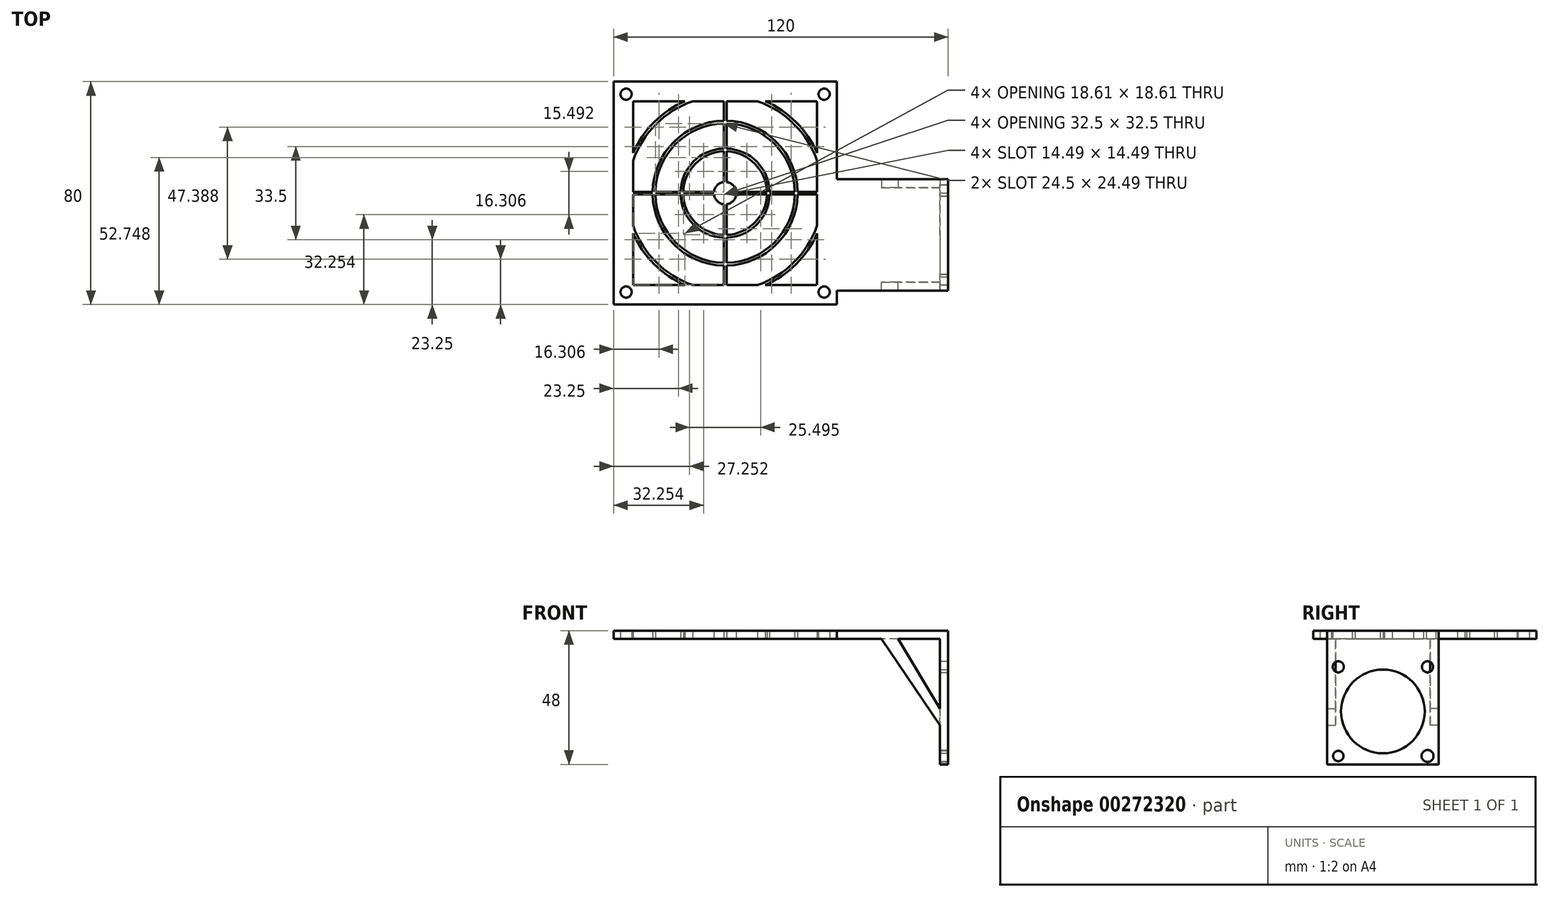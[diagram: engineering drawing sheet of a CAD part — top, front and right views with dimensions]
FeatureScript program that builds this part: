
annotation { "Feature Type Name" : "Feature", "Feature Type Description" : "" }
export const myFeature = defineFeature(function(context is Context, id is Id, definition is map)
    precondition{}
    {
        {
            var Q0;
            Q0=qCreatedBy(makeId("Top.planeOp"),FACE);
            var sketch = newSketch(context, id + "F0", { "sketchPlane" : qUnion([Q0])});
            skLineSegment(sketch, "E0.bottom", {"start": v(-80, 0) * mm, "end": v(0, 0) * mm});
            skLineSegment(sketch, "E0.top", {"start": v(-80, -80) * mm, "end": v(0, -80) * mm});
            skLineSegment(sketch, "E0.left", {"start": v(-80, 0) * mm, "end": v(-80, -80) * mm});
            skLineSegment(sketch, "E0.right", {"start": v(0, 0) * mm, "end": v(0, -80) * mm});
            skLineSegment(sketch, "E1", {"start": v(0, -35) * mm, "end": v(40, -35) * mm});
            skLineSegment(sketch, "E2", {"start": v(40, -35) * mm, "end": v(40, -75) * mm});
            skLineSegment(sketch, "E3", {"start": v(40, -75) * mm, "end": v(0, -75) * mm});
            skLineSegment(sketch, "E4", {"start": v(-80, -40) * mm, "end": v(0, -40) * mm, "construction": true});
            skLineSegment(sketch, "E5", {"start": v(40, -55) * mm, "end": v(0, -55) * mm, "construction": true});
            skLineSegment(sketch, "E6.0", {"start": v(-73, -7) * mm, "end": v(-7, -7) * mm});
            skLineSegment(sketch, "E6.1", {"start": v(-73, -7) * mm, "end": v(-73, -73) * mm});
            skLineSegment(sketch, "E6.2", {"start": v(-73, -73) * mm, "end": v(-7, -73) * mm});
            skLineSegment(sketch, "E6.3", {"start": v(-7, -7) * mm, "end": v(-7, -73) * mm});
            skCircle(sketch, "E7", {"center": v(-75.5, -4.5) * mm, "radius": 2 * mm});
            skCircle(sketch, "E8", {"center": v(-4.5, -4.5) * mm, "radius": 2 * mm});
            skCircle(sketch, "E9", {"center": v(-75.5, -75.5) * mm, "radius": 2 * mm});
            skCircle(sketch, "E10", {"center": v(-4.5, -75.5) * mm, "radius": 2 * mm});
            skLineSegment(sketch, "E11", {"start": v(-75.5, -4.5) * mm, "end": v(-4.5, -4.5) * mm, "construction": true});
            skLineSegment(sketch, "E12", {"start": v(-40, 0) * mm, "end": v(-40, -80) * mm, "construction": true});
            skPoint(sketch, "E13", {"position": v(-40, -4.5) * mm});
            skLineSegment(sketch, "E14", {"start": v(-75.5, -4.5) * mm, "end": v(-75.5, -75.5) * mm, "construction": true});
            skLineSegment(sketch, "E15", {"start": v(-75.5, -75.5) * mm, "end": v(-4.5, -75.5) * mm, "construction": true});
            skPoint(sketch, "E16", {"position": v(-75.5, -40) * mm});
            skSolve(sketch);
        }
        {
            var Q0;
            {var subQ4=sQuery(id+"F0.wireOp",EDGE,"E0.bottom");Q0=makeQuery(id+"F0.imprint","IMPRINT",FACE,{"disambiguationData":[TD([[makeQuery(id+"F0.imprint","IMPRINT",EDGE,{"derivedFrom":subQ4}),-1.0]])]});}
            var Q1;
            {var subQ0=sQuery(id+"F0.wireOp",EDGE,"E1");Q1=makeQuery(id+"F0.imprint","IMPRINT",FACE,{"disambiguationData":[TD([[makeQuery(id+"F0.imprint","IMPRINT",EDGE,{"derivedFrom":subQ0}),-1.0]])]});}
            extrude(context, id + "F1", {"entities" : qUnion([Q0, Q1]), "depth" : 3 * mm});
        }
        {
            var Q0;
            Q0=makeQuery(id+"F1.opExtrude","CAP_FACE",FACE,{"disambiguationData":[OSD([sQuery(id+"F0.wireOp",EDGE,"E0.bottom"),sQuery(id+"F0.wireOp",EDGE,"E0.top"),sQuery(id+"F0.wireOp",EDGE,"E0.left"),sQuery(id+"F0.wireOp",EDGE,"E0.right"),sQuery(id+"F0.wireOp",EDGE,"E1"),sQuery(id+"F0.wireOp",EDGE,"E2"),sQuery(id+"F0.wireOp",EDGE,"E3"),sQuery(id+"F0.wireOp",EDGE,"E6.0"),sQuery(id+"F0.wireOp",EDGE,"E6.1"),sQuery(id+"F0.wireOp",EDGE,"E6.2"),sQuery(id+"F0.wireOp",EDGE,"E6.3"),sQuery(id+"F0.wireOp",EDGE,"E7"),sQuery(id+"F0.wireOp",EDGE,"E8"),sQuery(id+"F0.wireOp",EDGE,"E9"),sQuery(id+"F0.wireOp",EDGE,"E10")])],"isStart":true});
            var sketch = newSketch(context, id + "F2", { "sketchPlane" : qUnion([Q0])});
            skLineSegment(sketch, "E17.bottom", {"start": v(40, 35) * mm, "end": v(37, 35) * mm});
            skLineSegment(sketch, "E17.top", {"start": v(40, 75) * mm, "end": v(37, 75) * mm});
            skLineSegment(sketch, "E17.left", {"start": v(40, 35) * mm, "end": v(40, 75) * mm});
            skLineSegment(sketch, "E17.right", {"start": v(37, 35) * mm, "end": v(37, 75) * mm});
            skSolve(sketch);
        }
        {
            var Q0;
            Q0=makeQuery(id+"F2.imprint","IMPRINT",FACE,{"disambiguationData":[TD([[makeQuery(id+"F2.imprint","IMPRINT",EDGE,{"derivedFrom":sQuery(id+"F2.wireOp",EDGE,"E17.bottom")}),1.0]])]});
            extrude(context, id + "F3", {"entities" : qUnion([Q0]), "operationType" : NewBodyOperationType.ADD, "depth" : 45 * mm});
        }
        {
            var Q0;
            Q0=makeQuery(id+"F3.boolean.opBoolean","MERGE",FACE,{"derivedFrom":[makeQuery(id+"F1.opExtrude","SWEPT_FACE",FACE,{"disambiguationData":[OSD([sQuery(id+"F0.wireOp",EDGE,"E2")])]}),makeQuery(id+"F3.opExtrude","SWEPT_FACE",FACE,{"disambiguationData":[OSD([sQuery(id+"F2.wireOp",EDGE,"E17.left")])]})]});
            var sketch = newSketch(context, id + "F4", { "sketchPlane" : qUnion([Q0])});
            skLineSegment(sketch, "E18", {"start": v(-55, -45) * mm, "end": v(-55, 3) * mm, "construction": true});
            skCircle(sketch, "E19", {"center": v(-71, -10) * mm, "radius": 2 * mm});
            skCircle(sketch, "E20", {"center": v(-39, -10) * mm, "radius": 2 * mm});
            skCircle(sketch, "E21", {"center": v(-71, -42) * mm, "radius": 1.86 * mm});
            skCircle(sketch, "E22", {"center": v(-39, -42) * mm, "radius": 2.14 * mm});
            skLineSegment(sketch, "E23", {"start": v(-71, -10) * mm, "end": v(-39, -10) * mm, "construction": true});
            skPoint(sketch, "E24", {"position": v(-55, -10) * mm});
            skLineSegment(sketch, "E25", {"start": v(-71, -10) * mm, "end": v(-71, -42) * mm, "construction": true});
            skLineSegment(sketch, "E26", {"start": v(-71, -42) * mm, "end": v(-39, -42) * mm, "construction": true});
            skLineSegment(sketch, "E27", {"start": v(-75, -26) * mm, "end": v(-35, -26) * mm, "construction": true});
            skPoint(sketch, "E27.startSnap0", {"position": v(-71, -26) * mm});
            skPoint(sketch, "E27.startSnap1", {"position": v(-75, -21) * mm});
            skCircle(sketch, "E28", {"center": v(-55, -26) * mm, "radius": 15 * mm});
            skSolve(sketch);
        }
        {
            var Q0;
            Q0=makeQuery(id+"F4.imprint","IMPRINT",FACE,{"disambiguationData":[TD([[makeQuery(id+"F4.imprint","IMPRINT",EDGE,{"derivedFrom":sQuery(id+"F4.wireOp",EDGE,"E19")}),1.0]])]});
            var Q1;
            Q1=makeQuery(id+"F4.imprint","IMPRINT",FACE,{"disambiguationData":[TD([[makeQuery(id+"F4.imprint","IMPRINT",EDGE,{"derivedFrom":sQuery(id+"F4.wireOp",EDGE,"E21")}),1.0]])]});
            var Q2;
            Q2=makeQuery(id+"F4.imprint","IMPRINT",FACE,{"disambiguationData":[TD([[makeQuery(id+"F4.imprint","IMPRINT",EDGE,{"derivedFrom":sQuery(id+"F4.wireOp",EDGE,"E28")}),1.0]])]});
            var Q3;
            Q3=makeQuery(id+"F4.imprint","IMPRINT",FACE,{"disambiguationData":[TD([[makeQuery(id+"F4.imprint","IMPRINT",EDGE,{"derivedFrom":sQuery(id+"F4.wireOp",EDGE,"E22")}),1.0]])]});
            var Q4;
            Q4=makeQuery(id+"F4.imprint","IMPRINT",FACE,{"disambiguationData":[TD([[makeQuery(id+"F4.imprint","IMPRINT",EDGE,{"derivedFrom":sQuery(id+"F4.wireOp",EDGE,"E20")}),1.0]])]});
            extrude(context, id + "F5", {"entities" : qUnion([Q0, Q1, Q2, Q3, Q4]), "operationType" : NewBodyOperationType.REMOVE, "oppositeDirection" : true, "depth" : 25 * mm});
        }
        {
            var Q0;
            Q0=makeQuery(id+"F1.opExtrude","CAP_FACE",FACE,{"disambiguationData":[OSD([sQuery(id+"F0.wireOp",EDGE,"E0.bottom"),sQuery(id+"F0.wireOp",EDGE,"E0.top"),sQuery(id+"F0.wireOp",EDGE,"E0.left"),sQuery(id+"F0.wireOp",EDGE,"E0.right"),sQuery(id+"F0.wireOp",EDGE,"E1"),sQuery(id+"F0.wireOp",EDGE,"E2"),sQuery(id+"F0.wireOp",EDGE,"E3"),sQuery(id+"F0.wireOp",EDGE,"E6.0"),sQuery(id+"F0.wireOp",EDGE,"E6.1"),sQuery(id+"F0.wireOp",EDGE,"E6.2"),sQuery(id+"F0.wireOp",EDGE,"E6.3"),sQuery(id+"F0.wireOp",EDGE,"E7"),sQuery(id+"F0.wireOp",EDGE,"E8"),sQuery(id+"F0.wireOp",EDGE,"E9"),sQuery(id+"F0.wireOp",EDGE,"E10")])],"isStart":true});
            var sketch = newSketch(context, id + "F6", { "sketchPlane" : qUnion([Q0])});
            skLineSegment(sketch, "E29", {"start": v(-73, 40) * mm, "end": v(-44, 40) * mm, "construction": true});
            skLineSegment(sketch, "E30", {"start": v(-73, 39.5) * mm, "end": v(-71.5, 39.5) * mm});
            skLineSegment(sketch, "E31", {"start": v(-73, 40.5) * mm, "end": v(-71, 40.5) * mm});
            skLineSegment(sketch, "E32.0", {"start": v(-73, 7) * mm, "end": v(-73, 73) * mm});
            skLineSegment(sketch, "E32.1", {"start": v(-73, 7) * mm, "end": v(-7, 7) * mm});
            skLineSegment(sketch, "E32.2", {"start": v(-7, 7) * mm, "end": v(-7, 73) * mm});
            skLineSegment(sketch, "E32.3", {"start": v(-73, 73) * mm, "end": v(-7, 73) * mm});
            skLineSegment(sketch, "E33", {"start": v(-40, 73) * mm, "end": v(-40, 44) * mm, "construction": true});
            skLineSegment(sketch, "E34", {"start": v(-40.5, 7) * mm, "end": v(-40.5, 9) * mm});
            skLineSegment(sketch, "E35", {"start": v(-39.5, 73) * mm, "end": v(-39.5, 71) * mm});
            skArc(sketch, "E36", {"start": v(-36.03, 40.5) * mm, "mid": v(-37.17, 42.83) * mm, "end": v(-39.5, 43.97) * mm});
            skLineSegment(sketch, "E37.trimOffspring", {"start": v(-40.5, 43.97) * mm, "end": v(-40.5, 49.99) * mm});
            skLineSegment(sketch, "E38.trimOffspring", {"start": v(-40, 39.5) * mm, "end": v(-39, 39.5) * mm, "construction": true});
            skLineSegment(sketch, "E39.trimOffspring", {"start": v(-41, 40.5) * mm, "end": v(-40, 40.5) * mm, "construction": true});
            skLineSegment(sketch, "E40.trimOffspring", {"start": v(-41, 40) * mm, "end": v(-40, 40) * mm, "construction": true});
            skLineSegment(sketch, "E41.trimOffspring", {"start": v(-36.03, 40.5) * mm, "end": v(-30.01, 40.5) * mm});
            skLineSegment(sketch, "E42.trimOffspring", {"start": v(-36, 40) * mm, "end": v(-7, 40) * mm, "construction": true});
            skLineSegment(sketch, "E43.trimOffspring", {"start": v(-36.03, 39.5) * mm, "end": v(-30.01, 39.5) * mm});
            skLineSegment(sketch, "E44.trimOffspring", {"start": v(-39.5, 36.03) * mm, "end": v(-39.5, 30.01) * mm});
            skLineSegment(sketch, "E45.trimOffspring", {"start": v(-40, 40.5) * mm, "end": v(-40, 40) * mm, "construction": true});
            skLineSegment(sketch, "E46.trimOffspring", {"start": v(-40, 36) * mm, "end": v(-40, 7) * mm, "construction": true});
            skArc(sketch, "E47", {"start": v(-39.5, 25) * mm, "mid": v(-29.4, 29.4) * mm, "end": v(-25, 39.5) * mm});
            skArc(sketch, "E48", {"start": v(-39.5, 24) * mm, "mid": v(-28.69, 28.69) * mm, "end": v(-24, 39.5) * mm});
            skArc(sketch, "E49", {"start": v(-39.5, 15) * mm, "mid": v(-22.32, 22.32) * mm, "end": v(-15, 39.5) * mm});
            skArc(sketch, "E50", {"start": v(-39.5, 14) * mm, "mid": v(-21.62, 21.62) * mm, "end": v(-14, 39.5) * mm});
            skLineSegment(sketch, "E51.trimOffspring", {"start": v(-39.5, 9) * mm, "end": v(-39.5, 7) * mm});
            skLineSegment(sketch, "E52.trimOffspring", {"start": v(-40.5, 10) * mm, "end": v(-40.5, 14) * mm});
            skLineSegment(sketch, "E53.trimOffspring", {"start": v(-39.5, 14) * mm, "end": v(-39.5, 10) * mm});
            skLineSegment(sketch, "E54.trimOffspring", {"start": v(-40.5, 15) * mm, "end": v(-40.5, 19) * mm});
            skLineSegment(sketch, "E55.trimOffspring", {"start": v(-39.5, 19) * mm, "end": v(-39.5, 15) * mm});
            skLineSegment(sketch, "E56.trimOffspring", {"start": v(-40.5, 20) * mm, "end": v(-40.5, 24) * mm});
            skLineSegment(sketch, "E57.trimOffspring", {"start": v(-39.5, 24) * mm, "end": v(-39.5, 20) * mm});
            skLineSegment(sketch, "E58.trimOffspring", {"start": v(-40.5, 25) * mm, "end": v(-40.5, 29.01) * mm});
            skLineSegment(sketch, "E59.trimOffspring", {"start": v(-39.5, 29.01) * mm, "end": v(-39.5, 25) * mm});
            skLineSegment(sketch, "E60.trimOffspring", {"start": v(-40.5, 30.01) * mm, "end": v(-40.5, 36.03) * mm});
            skLineSegment(sketch, "E61.trimOffspring", {"start": v(-39.5, 49.99) * mm, "end": v(-39.5, 43.97) * mm});
            skLineSegment(sketch, "E62.trimOffspring", {"start": v(-40.5, 50.99) * mm, "end": v(-40.5, 55) * mm});
            skLineSegment(sketch, "E63.trimOffspring", {"start": v(-40.5, 56) * mm, "end": v(-40.5, 60) * mm});
            skLineSegment(sketch, "E64.trimOffspring", {"start": v(-39.5, 55) * mm, "end": v(-39.5, 50.99) * mm});
            skLineSegment(sketch, "E65.trimOffspring", {"start": v(-39.5, 60) * mm, "end": v(-39.5, 56) * mm});
            skLineSegment(sketch, "E66.trimOffspring", {"start": v(-40.5, 61) * mm, "end": v(-40.5, 65) * mm});
            skLineSegment(sketch, "E67.trimOffspring", {"start": v(-39.5, 65) * mm, "end": v(-39.5, 61) * mm});
            skLineSegment(sketch, "E68.trimOffspring", {"start": v(-40.5, 66) * mm, "end": v(-40.5, 70) * mm});
            skLineSegment(sketch, "E69.trimOffspring", {"start": v(-39.5, 70) * mm, "end": v(-39.5, 66) * mm});
            skLineSegment(sketch, "E70.trimOffspring", {"start": v(-40.5, 71) * mm, "end": v(-40.5, 73) * mm});
            skLineSegment(sketch, "E71.trimOffspring", {"start": v(-29.01, 39.5) * mm, "end": v(-25, 39.5) * mm});
            skLineSegment(sketch, "E72.trimOffspring", {"start": v(-29.01, 40.5) * mm, "end": v(-25, 40.5) * mm});
            skLineSegment(sketch, "E73.trimOffspring", {"start": v(-24, 40.5) * mm, "end": v(-20, 40.5) * mm});
            skLineSegment(sketch, "E74.trimOffspring", {"start": v(-24, 39.5) * mm, "end": v(-20, 39.5) * mm});
            skLineSegment(sketch, "E75.trimOffspring", {"start": v(-19, 39.5) * mm, "end": v(-15, 39.5) * mm});
            skLineSegment(sketch, "E76.trimOffspring", {"start": v(-19, 40.5) * mm, "end": v(-15, 40.5) * mm});
            skLineSegment(sketch, "E77.trimOffspring", {"start": v(-14, 40.5) * mm, "end": v(-10, 40.5) * mm});
            skLineSegment(sketch, "E78.trimOffspring", {"start": v(-14, 39.5) * mm, "end": v(-10, 39.5) * mm});
            skLineSegment(sketch, "E79.trimOffspring", {"start": v(-9, 39.5) * mm, "end": v(-7, 39.5) * mm});
            skLineSegment(sketch, "E80.trimOffspring", {"start": v(-9, 40.5) * mm, "end": v(-7, 40.5) * mm});
            skLineSegment(sketch, "E81.trimOffspring", {"start": v(-49.99, 40.5) * mm, "end": v(-43.97, 40.5) * mm});
            skLineSegment(sketch, "E82.trimOffspring", {"start": v(-49.99, 39.5) * mm, "end": v(-43.97, 39.5) * mm});
            skLineSegment(sketch, "E83.trimOffspring", {"start": v(-55, 39.5) * mm, "end": v(-50.99, 39.5) * mm});
            skLineSegment(sketch, "E84.trimOffspring", {"start": v(-55, 40.5) * mm, "end": v(-50.99, 40.5) * mm});
            skLineSegment(sketch, "E85.trimOffspring", {"start": v(-60, 40.5) * mm, "end": v(-56, 40.5) * mm});
            skLineSegment(sketch, "E86.trimOffspring", {"start": v(-60, 39.5) * mm, "end": v(-56, 39.5) * mm});
            skLineSegment(sketch, "E87.trimOffspring", {"start": v(-65, 39.5) * mm, "end": v(-61, 39.5) * mm});
            skLineSegment(sketch, "E88.trimOffspring", {"start": v(-65, 40.5) * mm, "end": v(-61, 40.5) * mm});
            skLineSegment(sketch, "E89.trimOffspring", {"start": v(-70, 40.5) * mm, "end": v(-66, 40.5) * mm});
            skLineSegment(sketch, "E90.trimOffspring", {"start": v(-70, 39.5) * mm, "end": v(-66, 39.5) * mm});
            skArc(sketch, "E91.trimOffspring", {"start": v(-55, 39.5) * mm, "mid": v(-50.6, 29.4) * mm, "end": v(-40.5, 25) * mm});
            skArc(sketch, "E92.trimOffspring", {"start": v(-56, 39.5) * mm, "mid": v(-51.31, 28.69) * mm, "end": v(-40.5, 24) * mm});
            skArc(sketch, "E93.trimOffspring", {"start": v(-65, 39.5) * mm, "mid": v(-57.68, 22.32) * mm, "end": v(-40.5, 15) * mm});
            skArc(sketch, "E94.trimOffspring", {"start": v(-66, 39.5) * mm, "mid": v(-58.38, 21.62) * mm, "end": v(-40.5, 14) * mm});
            skArc(sketch, "E95.trimOffspring", {"start": v(-40.5, 55) * mm, "mid": v(-50.6, 50.6) * mm, "end": v(-55, 40.5) * mm});
            skArc(sketch, "E96.trimOffspring", {"start": v(-40.5, 56) * mm, "mid": v(-51.31, 51.31) * mm, "end": v(-56, 40.5) * mm});
            skArc(sketch, "E97.trimOffspring", {"start": v(-40.5, 65) * mm, "mid": v(-57.68, 57.68) * mm, "end": v(-65, 40.5) * mm});
            skArc(sketch, "E98.trimOffspring", {"start": v(-40.5, 66) * mm, "mid": v(-58.38, 58.38) * mm, "end": v(-66, 40.5) * mm});
            skArc(sketch, "E99.trimOffspring", {"start": v(-25, 40.5) * mm, "mid": v(-29.4, 50.6) * mm, "end": v(-39.5, 55) * mm});
            skArc(sketch, "E100.trimOffspring", {"start": v(-24, 40.5) * mm, "mid": v(-28.69, 51.31) * mm, "end": v(-39.5, 56) * mm});
            skArc(sketch, "E101.trimOffspring", {"start": v(-15, 40.5) * mm, "mid": v(-22.32, 57.68) * mm, "end": v(-39.5, 65) * mm});
            skArc(sketch, "E102.trimOffspring", {"start": v(-14, 40.5) * mm, "mid": v(-21.62, 58.38) * mm, "end": v(-39.5, 66) * mm});
            skArc(sketch, "E103.trimOffspring", {"start": v(-39.5, 36.03) * mm, "mid": v(-37.17, 37.17) * mm, "end": v(-36.03, 39.5) * mm});
            skArc(sketch, "E104.trimOffspring", {"start": v(-43.97, 39.5) * mm, "mid": v(-42.83, 37.17) * mm, "end": v(-40.5, 36.03) * mm});
            skArc(sketch, "E105.trimOffspring", {"start": v(-40.5, 43.97) * mm, "mid": v(-42.83, 42.83) * mm, "end": v(-43.97, 40.5) * mm});
            skArc(sketch, "E106", {"start": v(-7, 51.66) * mm, "mid": v(-15.25, 64.75) * mm, "end": v(-28.34, 73) * mm});
            skArc(sketch, "E107", {"start": v(-7, 54.39) * mm, "mid": v(-14.54, 65.46) * mm, "end": v(-25.61, 73) * mm});
            skArc(sketch, "E108.trimOffspring", {"start": v(-54.39, 73) * mm, "mid": v(-65.46, 65.46) * mm, "end": v(-73, 54.39) * mm});
            skArc(sketch, "E109.trimOffspring", {"start": v(-51.66, 73) * mm, "mid": v(-64.75, 64.75) * mm, "end": v(-73, 51.66) * mm});
            skArc(sketch, "E110.trimOffspring", {"start": v(-73, 25.61) * mm, "mid": v(-65.46, 14.54) * mm, "end": v(-54.39, 7) * mm});
            skArc(sketch, "E111.trimOffspring", {"start": v(-73, 28.34) * mm, "mid": v(-64.75, 15.25) * mm, "end": v(-51.66, 7) * mm});
            skArc(sketch, "E112.trimOffspring", {"start": v(-25.61, 7) * mm, "mid": v(-14.54, 14.54) * mm, "end": v(-7, 25.61) * mm});
            skArc(sketch, "E113.trimOffspring", {"start": v(-28.34, 7) * mm, "mid": v(-15.25, 15.25) * mm, "end": v(-7, 28.34) * mm});
            skLineSegment(sketch, "E114", {"start": v(-39.5, 60) * mm, "end": v(-39.5, 61) * mm});
            skLineSegment(sketch, "E115", {"start": v(-40.5, 60) * mm, "end": v(-40.5, 61) * mm});
            skLineSegment(sketch, "E116", {"start": v(-40.5, 70) * mm, "end": v(-40.5, 71) * mm});
            skLineSegment(sketch, "E117", {"start": v(-39.5, 70) * mm, "end": v(-39.5, 71) * mm});
            skLineSegment(sketch, "E118", {"start": v(-61, 39.5) * mm, "end": v(-60, 39.5) * mm});
            skLineSegment(sketch, "E119", {"start": v(-60, 40.5) * mm, "end": v(-61, 40.5) * mm});
            skLineSegment(sketch, "E120", {"start": v(-70, 39.5) * mm, "end": v(-71.5, 39.5) * mm});
            skLineSegment(sketch, "E121", {"start": v(-70, 40.5) * mm, "end": v(-71, 40.5) * mm});
            skLineSegment(sketch, "E122", {"start": v(-40.5, 20) * mm, "end": v(-40.5, 19) * mm});
            skLineSegment(sketch, "E123", {"start": v(-39.5, 19) * mm, "end": v(-39.5, 20) * mm});
            skLineSegment(sketch, "E124", {"start": v(-40.5, 9) * mm, "end": v(-40.5, 10) * mm});
            skLineSegment(sketch, "E125", {"start": v(-39.5, 9) * mm, "end": v(-39.5, 10) * mm});
            skLineSegment(sketch, "E126", {"start": v(-19, 39.5) * mm, "end": v(-20, 39.5) * mm});
            skLineSegment(sketch, "E127", {"start": v(-20, 40.5) * mm, "end": v(-19, 40.5) * mm});
            skLineSegment(sketch, "E128", {"start": v(-9, 39.5) * mm, "end": v(-10, 39.5) * mm});
            skLineSegment(sketch, "E129", {"start": v(-10, 40.5) * mm, "end": v(-9, 40.5) * mm});
            skLineSegment(sketch, "E130", {"start": v(-30.01, 40.5) * mm, "end": v(-29.01, 40.5) * mm});
            skLineSegment(sketch, "E131", {"start": v(-30.01, 39.5) * mm, "end": v(-29.01, 39.5) * mm});
            skLineSegment(sketch, "E132", {"start": v(-40.5, 30.01) * mm, "end": v(-40.5, 29.01) * mm});
            skLineSegment(sketch, "E133", {"start": v(-39.5, 29.01) * mm, "end": v(-39.5, 30.01) * mm});
            skLineSegment(sketch, "E134", {"start": v(-49.99, 39.5) * mm, "end": v(-50.99, 39.5) * mm});
            skLineSegment(sketch, "E135", {"start": v(-50.99, 40.5) * mm, "end": v(-49.99, 40.5) * mm});
            skLineSegment(sketch, "E136", {"start": v(-40.5, 49.99) * mm, "end": v(-40.5, 50.99) * mm});
            skLineSegment(sketch, "E137", {"start": v(-39.5, 49.99) * mm, "end": v(-39.5, 50.99) * mm});
            skSolve(sketch);
        }
        {
            var Q0;
            {var subQ5=sQuery(id+"F6.wireOp",EDGE,"E30");Q0=makeQuery(id+"F6.imprint","IMPRINT",FACE,{"disambiguationData":[TD([[makeQuery(id+"F6.imprint","IMPRINT",EDGE,{"derivedFrom":subQ5}),1.0]])]});}
            var Q1;
            {var subQ0=sQuery(id+"F6.wireOp",EDGE,"E112.trimOffspring");Q1=makeQuery(id+"F6.imprint","IMPRINT",FACE,{"disambiguationData":[TD([[makeQuery(id+"F6.imprint","IMPRINT",EDGE,{"derivedFrom":subQ0}),1.0]])]});}
            var Q2;
            {var subQ0=sQuery(id+"F6.wireOp",EDGE,"E106");Q2=makeQuery(id+"F6.imprint","IMPRINT",FACE,{"disambiguationData":[TD([[makeQuery(id+"F6.imprint","IMPRINT",EDGE,{"derivedFrom":subQ0}),-1.0]])]});}
            var Q3;
            {var subQ0=sQuery(id+"F6.wireOp",EDGE,"E108.trimOffspring");Q3=makeQuery(id+"F6.imprint","IMPRINT",FACE,{"disambiguationData":[TD([[makeQuery(id+"F6.imprint","IMPRINT",EDGE,{"derivedFrom":subQ0}),1.0]])]});}
            var Q4;
            {var subQ0=sQuery(id+"F6.wireOp",EDGE,"E110.trimOffspring");Q4=makeQuery(id+"F6.imprint","IMPRINT",FACE,{"disambiguationData":[TD([[makeQuery(id+"F6.imprint","IMPRINT",EDGE,{"derivedFrom":subQ0}),1.0]])]});}
            var Q5;
            Q5=makeQuery(id+"F1.opExtrude","CAP_FACE",FACE,{"disambiguationData":[OSD([sQuery(id+"F0.wireOp",EDGE,"E0.bottom"),sQuery(id+"F0.wireOp",EDGE,"E0.top"),sQuery(id+"F0.wireOp",EDGE,"E0.left"),sQuery(id+"F0.wireOp",EDGE,"E0.right"),sQuery(id+"F0.wireOp",EDGE,"E1"),sQuery(id+"F0.wireOp",EDGE,"E2"),sQuery(id+"F0.wireOp",EDGE,"E3"),sQuery(id+"F0.wireOp",EDGE,"E6.0"),sQuery(id+"F0.wireOp",EDGE,"E6.1"),sQuery(id+"F0.wireOp",EDGE,"E6.2"),sQuery(id+"F0.wireOp",EDGE,"E6.3"),sQuery(id+"F0.wireOp",EDGE,"E7"),sQuery(id+"F0.wireOp",EDGE,"E8"),sQuery(id+"F0.wireOp",EDGE,"E9"),sQuery(id+"F0.wireOp",EDGE,"E10")])],"isStart":false});
            extrude(context, id + "F7", {"entities" : qUnion([Q0, Q1, Q2, Q3, Q4]), "operationType" : NewBodyOperationType.ADD, "endBound" : BoundingType.UP_TO_SURFACE, "oppositeDirection" : true, "endBoundEntityFace" : qUnion([Q5]), "depth" : 1 * mm, "offsetDistance" : 25 * mm});
        }
        {
            var Q0;
            Q0=makeQuery(id+"F3.boolean.opBoolean","MERGE",FACE,{"derivedFrom":[makeQuery(id+"F1.opExtrude","SWEPT_FACE",FACE,{"disambiguationData":[OSD([sQuery(id+"F0.wireOp",EDGE,"E1")])]}),makeQuery(id+"F3.opExtrude","SWEPT_FACE",FACE,{"disambiguationData":[OSD([sQuery(id+"F2.wireOp",EDGE,"E17.bottom")])]})]});
            cPlane(context, id + "F8", {"entities" : qUnion([Q0]), "cplaneType" : CPlaneType.OFFSET, "offset" : 3 * mm, "oppositeDirection" : true, "width" : 150 * mm, "height" : 150 * mm});
        }
        {
            var Q0;
            Q0=qCreatedBy(id+"F8.planeOp",FACE);
            var sketch = newSketch(context, id + "F9", { "sketchPlane" : qUnion([Q0])});
            skLineSegment(sketch, "E138", {"start": v(-37, -25) * mm, "end": v(-22, 0) * mm});
            skLineSegment(sketch, "E139", {"start": v(-22, 0) * mm, "end": v(-16, 0) * mm});
            skLineSegment(sketch, "E140", {"start": v(-16, 0) * mm, "end": v(-37, -31) * mm});
            skLineSegment(sketch, "E141", {"start": v(-37, -31) * mm, "end": v(-37, -25) * mm});
            skSolve(sketch);
        }
        {
            var Q0;
            Q0=makeQuery(id+"F9.imprint","IMPRINT",FACE,{"disambiguationData":[TD([[makeQuery(id+"F9.imprint","IMPRINT",EDGE,{"derivedFrom":sQuery(id+"F9.wireOp",EDGE,"E138")}),-1.0]])]});
            extrude(context, id + "F10", {"entities" : qUnion([Q0]), "depth" : 3 * mm});
        }
        {
            var Q0;
            Q0=makeQuery(id+"F3.boolean.opBoolean","MERGE",FACE,{"derivedFrom":[makeQuery(id+"F1.opExtrude","SWEPT_FACE",FACE,{"disambiguationData":[OSD([sQuery(id+"F0.wireOp",EDGE,"E3")])]}),makeQuery(id+"F3.opExtrude","SWEPT_FACE",FACE,{"disambiguationData":[OSD([sQuery(id+"F2.wireOp",EDGE,"E17.top")])]})]});
            cPlane(context, id + "F11", {"entities" : qUnion([Q0]), "cplaneType" : CPlaneType.OFFSET, "offset" : 20 * mm, "oppositeDirection" : true, "width" : 150 * mm, "height" : 150 * mm});
        }
        {
            var Q0;
            Q0=makeQuery(id+"F10.opExtrude","SWEPT_BODY",BODY,{"disambiguationData":[OSD([sQuery(id+"F9.wireOp",EDGE,"E138"),sQuery(id+"F9.wireOp",EDGE,"E139"),sQuery(id+"F9.wireOp",EDGE,"E140"),sQuery(id+"F9.wireOp",EDGE,"E141")])]});
            var Q1;
            Q1=qCreatedBy(id+"F11.planeOp",FACE);
            mirror(context, id + "F12", {"operationType" : NewBodyOperationType.ADD, "entities" : qUnion([Q0]), "mirrorPlane" : qUnion([Q1])});
        }
        {
            var Q0;
            Q0=makeQuery(id+"F1.opExtrude","SWEPT_FACE",FACE,{"disambiguationData":[OSD([sQuery(id+"F0.wireOp",EDGE,"E0.left")])]});
            cPlane(context, id + "F13", {"entities" : qUnion([Q0]), "cplaneType" : CPlaneType.OFFSET, "offset" : 25 * mm, "width" : 150 * mm, "height" : 150 * mm});
        }
        {
            var Q0;
            Q0=makeQuery(id+"F1.opExtrude","SWEPT_BODY",BODY,{"disambiguationData":[OSD([sQuery(id+"F0.wireOp",EDGE,"E0.bottom"),sQuery(id+"F0.wireOp",EDGE,"E0.top"),sQuery(id+"F0.wireOp",EDGE,"E0.left"),sQuery(id+"F0.wireOp",EDGE,"E0.right"),sQuery(id+"F0.wireOp",EDGE,"E1"),sQuery(id+"F0.wireOp",EDGE,"E2"),sQuery(id+"F0.wireOp",EDGE,"E3"),sQuery(id+"F0.wireOp",EDGE,"E6.0"),sQuery(id+"F0.wireOp",EDGE,"E6.1"),sQuery(id+"F0.wireOp",EDGE,"E6.2"),sQuery(id+"F0.wireOp",EDGE,"E6.3"),sQuery(id+"F0.wireOp",EDGE,"E7"),sQuery(id+"F0.wireOp",EDGE,"E8"),sQuery(id+"F0.wireOp",EDGE,"E9"),sQuery(id+"F0.wireOp",EDGE,"E10")])]});
            var Q1;
            Q1=qCreatedBy(id+"F13.planeOp",FACE);
            mirror(context, id + "F14", {"entities" : qUnion([Q0]), "mirrorPlane" : qUnion([Q1])});
        }
        {
            var Q0;
            Q0=makeQuery(id+"F14.opPattern","COPY",FACE,{"derivedFrom":makeQuery(id+"F3.boolean.opBoolean","MERGE",FACE,{"derivedFrom":[makeQuery(id+"F1.opExtrude","SWEPT_FACE",FACE,{"disambiguationData":[OSD([sQuery(id+"F0.wireOp",EDGE,"E2")])]}),makeQuery(id+"F3.opExtrude","SWEPT_FACE",FACE,{"disambiguationData":[OSD([sQuery(id+"F2.wireOp",EDGE,"E17.left")])]})]}),"instanceName":"1"});
            var Q1;
            {var subQ0=sQuery(id+"F0.wireOp",EDGE,"E0.right");Q1=makeQuery(id+"F14.opPattern","COPY",FACE,{"derivedFrom":makeQuery(id+"F1.opExtrude","SWEPT_FACE",FACE,{"disambiguationData":[OSD([subQ0]),TDD([makeQuery(id+"F0.imprint","IMPRINT",EDGE,{"disambiguationData":[TD([[makeQuery(id+"F0.imprint","INTERSECT",VERTEX,{"derivedFrom":[sQuery(id+"F0.wireOp",EDGE,"E0.bottom"),subQ0]}),-1.0]])],"derivedFrom":subQ0})])]}),"instanceName":"1"});}
            extrude(context, id + "F15", {"entities" : qUnion([Q0]), "operationType" : NewBodyOperationType.REMOVE, "endBound" : BoundingType.UP_TO_SURFACE, "oppositeDirection" : true, "depth" : 25 * mm, "endBoundEntityFace" : qUnion([Q1]), "offsetDistance" : 25 * mm});
        }
        {
            var Q0;
            Q0=makeQuery(id+"F15.boolean.opBoolean","SPLIT",BODY,{"disambiguationData":[OD(2.0)],"derivedFrom":makeQuery(id+"F14.opPattern","COPY",BODY,{"derivedFrom":makeQuery(id+"F1.opExtrude","SWEPT_BODY",BODY,{"disambiguationData":[OSD([sQuery(id+"F0.wireOp",EDGE,"E0.bottom"),sQuery(id+"F0.wireOp",EDGE,"E0.top"),sQuery(id+"F0.wireOp",EDGE,"E0.left"),sQuery(id+"F0.wireOp",EDGE,"E0.right"),sQuery(id+"F0.wireOp",EDGE,"E1"),sQuery(id+"F0.wireOp",EDGE,"E2"),sQuery(id+"F0.wireOp",EDGE,"E3"),sQuery(id+"F0.wireOp",EDGE,"E6.0"),sQuery(id+"F0.wireOp",EDGE,"E6.1"),sQuery(id+"F0.wireOp",EDGE,"E6.2"),sQuery(id+"F0.wireOp",EDGE,"E6.3"),sQuery(id+"F0.wireOp",EDGE,"E7"),sQuery(id+"F0.wireOp",EDGE,"E8"),sQuery(id+"F0.wireOp",EDGE,"E9"),sQuery(id+"F0.wireOp",EDGE,"E10")])]}),"instanceName":"1"})});
            var Q1;
            Q1=makeQuery(id+"F15.boolean.opBoolean","SPLIT",BODY,{"disambiguationData":[OD(1.0)],"derivedFrom":makeQuery(id+"F14.opPattern","COPY",BODY,{"derivedFrom":makeQuery(id+"F1.opExtrude","SWEPT_BODY",BODY,{"disambiguationData":[OSD([sQuery(id+"F0.wireOp",EDGE,"E0.bottom"),sQuery(id+"F0.wireOp",EDGE,"E0.top"),sQuery(id+"F0.wireOp",EDGE,"E0.left"),sQuery(id+"F0.wireOp",EDGE,"E0.right"),sQuery(id+"F0.wireOp",EDGE,"E1"),sQuery(id+"F0.wireOp",EDGE,"E2"),sQuery(id+"F0.wireOp",EDGE,"E3"),sQuery(id+"F0.wireOp",EDGE,"E6.0"),sQuery(id+"F0.wireOp",EDGE,"E6.1"),sQuery(id+"F0.wireOp",EDGE,"E6.2"),sQuery(id+"F0.wireOp",EDGE,"E6.3"),sQuery(id+"F0.wireOp",EDGE,"E7"),sQuery(id+"F0.wireOp",EDGE,"E8"),sQuery(id+"F0.wireOp",EDGE,"E9"),sQuery(id+"F0.wireOp",EDGE,"E10")])]}),"instanceName":"1"})});
            deleteBodies(context, id + "F16", {"entities" : qUnion([Q0, Q1])});
        }
    });
